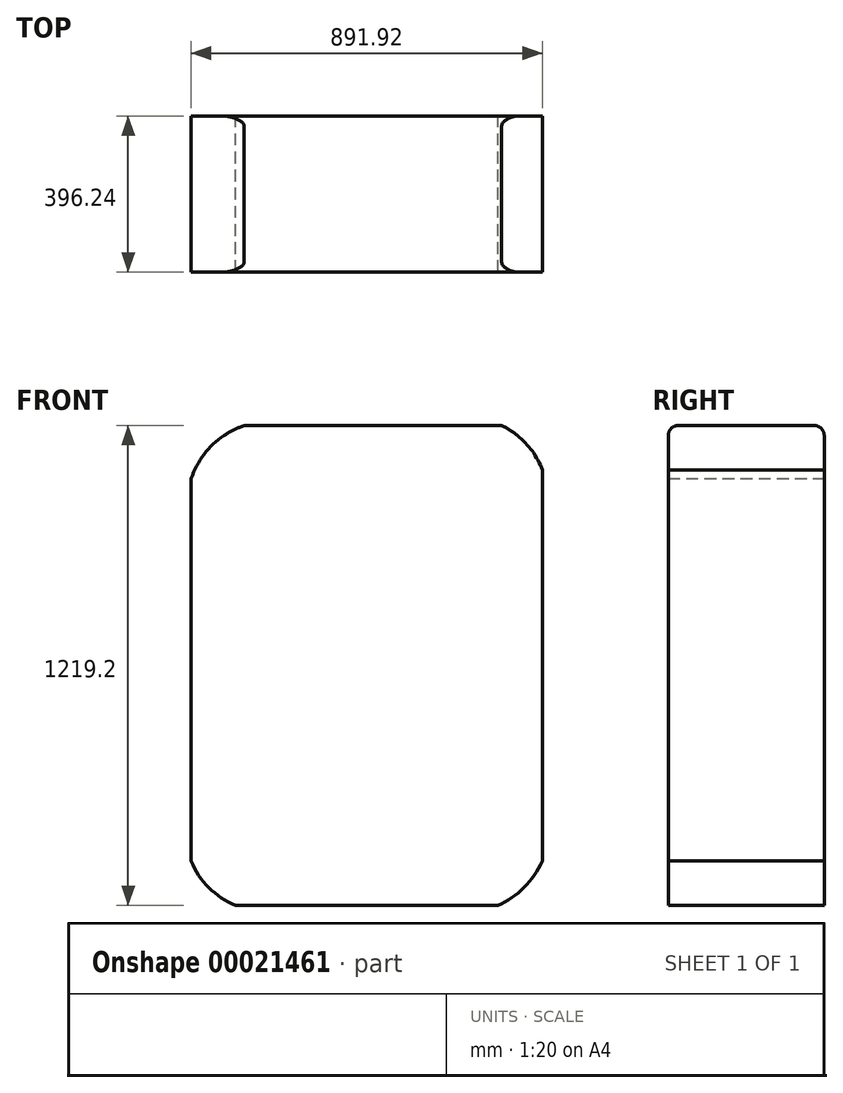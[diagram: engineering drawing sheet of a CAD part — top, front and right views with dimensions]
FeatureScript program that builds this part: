
annotation { "Feature Type Name" : "Feature", "Feature Type Description" : "" }
export const myFeature = defineFeature(function(context is Context, id is Id, definition is map)
    precondition{}
    {
        {
            var Q0;
            Q0=qCreatedBy(makeId("Front.planeOp"),FACE);
            var sketch = newSketch(context, id + "F0", { "sketchPlane" : qUnion([Q0])});
            skLineSegment(sketch, "E0.bottom", {"start": v(-310.46, 596.75) * mm, "end": v(343.52, 596.75) * mm});
            skLineSegment(sketch, "E0.top", {"start": v(-332.44, -622.45) * mm, "end": v(334.14, -622.45) * mm});
            skLineSegment(sketch, "E0.left", {"start": v(-445.11, 462.1) * mm, "end": v(-445.11, -509.77) * mm});
            skLineSegment(sketch, "E0.right", {"start": v(446.81, 484.08) * mm, "end": v(446.81, -509.77) * mm});
            skArc(sketch, "E1", {"start": v(446.81, 484.08) * mm, "mid": v(406.16, 550.5) * mm, "end": v(343.52, 596.75) * mm});
            skArc(sketch, "E2", {"start": v(-310.46, 596.75) * mm, "mid": v(-393.55, 545.2) * mm, "end": v(-445.11, 462.1) * mm});
            skArc(sketch, "E3", {"start": v(-445.11, -509.77) * mm, "mid": v(-400.28, -577.61) * mm, "end": v(-332.44, -622.45) * mm});
            skArc(sketch, "E4", {"start": v(334.14, -622.45) * mm, "mid": v(400.9, -576.54) * mm, "end": v(446.81, -509.77) * mm});
            skPoint(sketch, "E5.orphan", {"position": v(446.81, 596.75) * mm});
            skPoint(sketch, "E6.orphan", {"position": v(-445.11, -622.45) * mm});
            skPoint(sketch, "E7.orphan", {"position": v(446.81, -622.45) * mm});
            skSolve(sketch);
        }
        {
            var Q0;
            Q0=makeQuery(id+"F0.imprint","IMPRINT",FACE,{"disambiguationData":[TD([[makeQuery(id+"F0.imprint","IMPRINT",EDGE,{"derivedFrom":sQuery(id+"F0.wireOp",EDGE,"E0.bottom")}),-1.0]])]});
            extrude(context, id + "F1", {"entities" : qUnion([Q0]), "depth" : 396.24 * mm});
        }
        {
            var Q0;
            Q0=makeQuery(id+"F1.opExtrude","CAP_EDGE",EDGE,{"disambiguationData":[OSD([sQuery(id+"F0.wireOp",EDGE,"E0.bottom")])],"isStart":false});
            fillet(context, id + "F2", {"entities" : qUnion([Q0]), "radius" : 25.4 * mm, "tangentPropagation" : true, "allowEdgeOverflow" : false});
        }
        {
            var Q0;
            Q0=makeQuery(id+"F1.opExtrude","CAP_EDGE",EDGE,{"disambiguationData":[OSD([sQuery(id+"F0.wireOp",EDGE,"E0.bottom")])],"isStart":true});
            fillet(context, id + "F3", {"entities" : qUnion([Q0]), "radius" : 25.4 * mm, "tangentPropagation" : true, "allowEdgeOverflow" : false});
        }
    });
